# Revit family: 24-RHLI-60
name_source: partatom
category: Plumbing Fixtures
units: mm (PartAtom-declared; Revit-internal decimal feet)

## family parameters
Always vertical = Yes
Cut with Voids When Loaded = No
OmniClass Number = 23.45.00.00
OmniClass Title = Sanitary, Laundry, and Cleaning Equipment
Part Type = Normal
Room Calculation Point = No
Round Connector Dimension = Use Diameter
Shared = No
Work Plane-Based = No

## types (2) — shared parameters
Accessories = Hydraulic Seal 0,052 gal; Includes Setting Maintenance Tool
Brass Chromed = Brass
Cast Iron Cover = Iron, Cast
Data Sheet = http://helvex.com
Default Elevation = 0.000"
Description = Strainer with Contour Drain for Ceramic Insert
Features = Rectangular Strainer A Mouth; With Drainage Contour; 0,75" Installation Adjustment
Installation Thread = 2" - 11 ½ NPSM; Use A Ceramic Insert Of 10,6 x 2,36 x 0,39"
Manufacturer = HELVEX
Materials = Against Chrome Finish; Base Cylindrical Gray Cast Iron ASTM A 48 Class 25
Model = 24-RHLI
To Dislodge Volume of Flow = 9.2 gal/min
Type Comments = Drains
URL = http://helvex.com

## type names (no varying parameters)
- 24-RHLI
- 24-RHLI-60

## geometry (parser evidence)
native form markers: Sweep x3
no freeform markers — native parametric forms only
